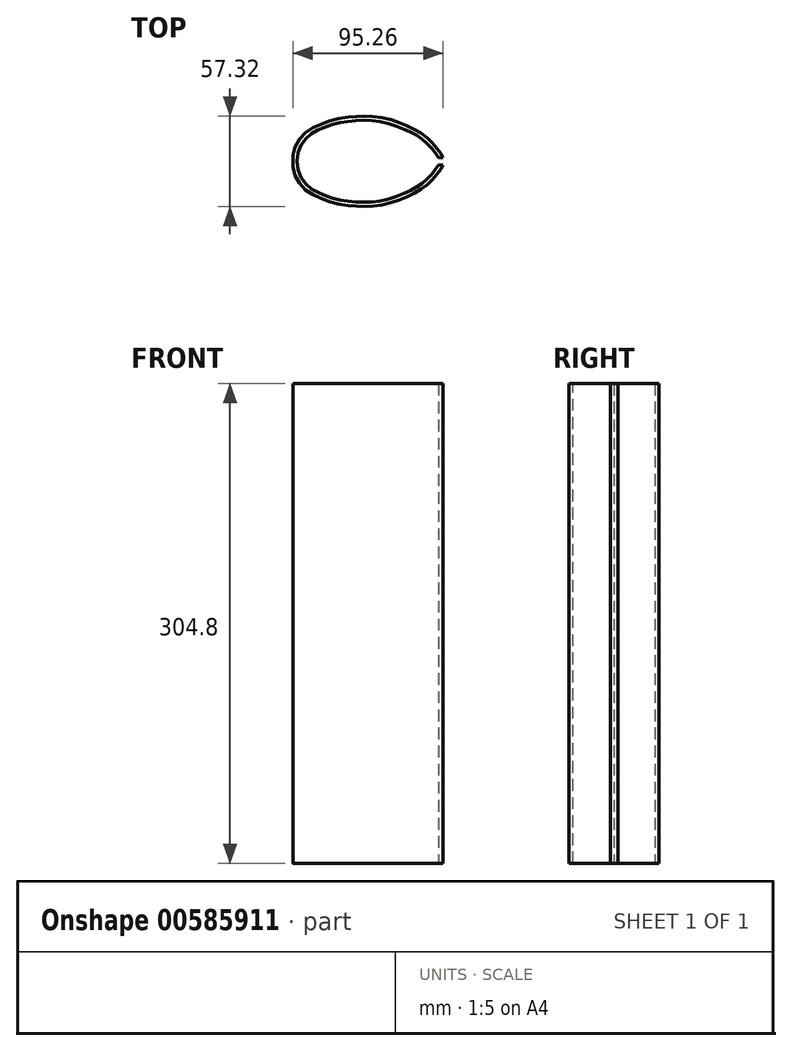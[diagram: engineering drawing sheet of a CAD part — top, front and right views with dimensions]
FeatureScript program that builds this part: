
annotation { "Feature Type Name" : "Feature", "Feature Type Description" : "" }
export const myFeature = defineFeature(function(context is Context, id is Id, definition is map)
    precondition{}
    {
        {
            var Q0;
            Q0=qCreatedBy(makeId("Top.planeOp"),FACE);
            var sketch = newSketch(context, id + "F0", { "sketchPlane" : qUnion([Q0])});
            skPoint(sketch, "E0", {"position": v(-43.82, 0) * mm});
            skSolve(sketch);
        }
        {
            var Q0;
            Q0=qCreatedBy(makeId("Top.planeOp"),FACE);
            var sketch = newSketch(context, id + "F1", { "sketchPlane" : qUnion([Q0])});
            skPoint(sketch, "E1", {"position": v(51.44, 0) * mm});
            skSolve(sketch);
        }
        {
            var Q0;
            Q0=qCreatedBy(makeId("Top.planeOp"),FACE);
            var sketch = newSketch(context, id + "F2", { "sketchPlane" : qUnion([Q0])});
            skPoint(sketch, "E2", {"position": v(0, 28.58) * mm});
            skSolve(sketch);
        }
        {
            var Q0;
            Q0=qCreatedBy(makeId("Top.planeOp"),FACE);
            var sketch = newSketch(context, id + "F3", { "sketchPlane" : qUnion([Q0])});
            skPoint(sketch, "E3", {"position": v(22.07, 0) * mm});
            skSolve(sketch);
        }
        {
            var Q0;
            Q0=qCreatedBy(makeId("Top.planeOp"),FACE);
            var sketch = newSketch(context, id + "F4", { "sketchPlane" : qUnion([Q0])});
            skPoint(sketch, "E4", {"position": v(14.86, 19.05) * mm});
            skSolve(sketch);
        }
        {
            var Q0;
            Q0=qCreatedBy(makeId("Top.planeOp"),FACE);
            var sketch = newSketch(context, id + "F5", { "sketchPlane" : qUnion([Q0])});
            skPoint(sketch, "E5", {"position": v(51.44, 2.39) * mm});
            skSolve(sketch);
        }
        {
            var Q0;
            Q0=qCreatedBy(makeId("Top.planeOp"),FACE);
            var sketch = newSketch(context, id + "F6", { "sketchPlane" : qUnion([Q0])});
            skArc(sketch, "E6", {"start": v(0, 28.58) * mm, "mid": v(-19.2, 25.91) * mm, "end": v(-36.96, 18.13) * mm});
            skSolve(sketch);
        }
        {
            var Q0;
            Q0=qCreatedBy(makeId("Top.planeOp"),FACE);
            var sketch = newSketch(context, id + "F7", { "sketchPlane" : qUnion([Q0])});
            skPoint(sketch, "E7", {"position": v(0, 25.04) * mm});
            skSolve(sketch);
        }
        {
            var Q0;
            Q0=qCreatedBy(makeId("Top.planeOp"),FACE);
            var sketch = newSketch(context, id + "F8", { "sketchPlane" : qUnion([Q0])});
            skLineSegment(sketch, "E8.bottom", {"start": v(46.93, 0) * mm, "end": v(59.21, 0) * mm});
            skLineSegment(sketch, "E8.top", {"start": v(46.93, 2.39) * mm, "end": v(59.21, 2.39) * mm});
            skLineSegment(sketch, "E8.left", {"start": v(46.93, 0) * mm, "end": v(46.93, 2.39) * mm});
            skLineSegment(sketch, "E8.right", {"start": v(59.21, 0) * mm, "end": v(59.21, 2.39) * mm});
            skSolve(sketch);
        }
        {
            var Q0;
            Q0=qCreatedBy(makeId("Top.planeOp"),FACE);
            var sketch = newSketch(context, id + "F9", { "sketchPlane" : qUnion([Q0])});
            skFitSpline(sketch, "E9", {"points": [v(-43.82, 0) * mm, v(-42.29, 8.43) * mm, v(-38.7, 14.76) * mm, v(-33.64, 19.55) * mm, v(-28, 22.56) * mm, v(-21.88, 24.98) * mm, v(-13.72, 27.17) * mm, v(-5.78, 28.23) * mm, v(0, 28.56) * mm, v(5.9, 28.37) * mm, v(12.54, 27.57) * mm, v(19.9, 25.73) * mm, v(25.6, 23.7) * mm, v(31.67, 20.94) * mm, v(36.27, 18.37) * mm, v(40.88, 15.08) * mm, v(44.19, 12) * mm, v(47.1, 8.7) * mm, v(49.61, 5.46) * mm, v(51.44, 2.39) * mm], "startDerivative": vector(2.54, 145.05) * mm, "endDerivative": vector(28.25, -58.97) * mm});
            skSolve(sketch);
        }
        {
            var Q0;
            Q0=qCreatedBy(makeId("Top.planeOp"),FACE);
            var sketch = newSketch(context, id + "F10", { "sketchPlane" : qUnion([Q0])});
            skFitSpline(sketch, "E10.0", {"points": [v(-41.28, 0.01) * mm, v(-41.28, 1.36) * mm, v(-41.03, 4) * mm, v(-40.15, 7.05) * mm, v(-39.2, 9.27) * mm, v(-38.37, 10.83) * mm, v(-37.4, 12.3) * mm, v(-36.33, 13.7) * mm, v(-35.14, 15) * mm, v(-33.86, 16.2) * mm, v(-32.73, 17.1) * mm, v(-31.81, 17.72) * mm, v(-30.86, 18.32) * mm, v(-29.62, 19) * mm, v(-28.3, 19.64) * mm, v(-27.23, 20.13) * mm, v(-26.13, 20.61) * mm, v(-24.77, 21.2) * mm, v(-23.09, 21.86) * mm, v(-21.33, 22.5) * mm, v(-19.46, 23.1) * mm, v(-17.5, 23.69) * mm, v(-15.47, 24.21) * mm, v(-13.76, 24.59) * mm, v(-12.4, 24.84) * mm, v(-11.02, 25.07) * mm, v(-9.32, 25.31) * mm, v(-7.32, 25.54) * mm, v(-5.4, 25.72) * mm, v(-3.63, 25.87) * mm, v(-1.94, 25.97) * mm, v(-0.3, 26.03) * mm, v(1.37, 26.03) * mm, v(3.08, 25.99) * mm, v(4.84, 25.9) * mm, v(6.62, 25.78) * mm, v(8.4, 25.61) * mm, v(10.2, 25.39) * mm, v(12.04, 25.1) * mm, v(13.96, 24.7) * mm, v(15.9, 24.22) * mm, v(17.81, 23.7) * mm, v(19.62, 23.16) * mm, v(21.27, 22.62) * mm, v(22.87, 22.06) * mm, v(24.47, 21.43) * mm, v(26.17, 20.71) * mm, v(27.9, 19.94) * mm, v(29.32, 19.27) * mm, v(30.39, 18.75) * mm, v(31.4, 18.23) * mm, v(32.59, 17.6) * mm, v(33.71, 16.96) * mm, v(34.62, 16.41) * mm, v(35.54, 15.83) * mm, v(36.71, 15.04) * mm, v(37.86, 14.22) * mm, v(38.73, 13.55) * mm, v(39.56, 12.9) * mm, v(40.49, 12.1) * mm, v(41.51, 11.12) * mm, v(42.5, 10.1) * mm, v(43.5, 9) * mm, v(44.33, 8.04) * mm, v(44.98, 7.28) * mm, v(45.61, 6.52) * mm, v(46.2, 5.8) * mm, v(46.77, 5.07) * mm, v(47.18, 4.52) * mm, v(47.57, 3.95) * mm, v(47.96, 3.36) * mm, v(48.33, 2.77) * mm, v(48.67, 2.2) * mm, v(48.95, 1.68) * mm, v(49.09, 1.4) * mm, v(49.14, 1.3) * mm]});
            skSolve(sketch);
        }
        {
            var Q0;
            Q0=qCreatedBy(makeId("Top.planeOp"),FACE);
            var sketch = newSketch(context, id + "F11", { "sketchPlane" : qUnion([Q0])});
            skArc(sketch, "E11", {"start": v(28.78, 19.52) * mm, "mid": v(23.8, 10.32) * mm, "end": v(22.07, 0) * mm});
            skSolve(sketch);
        }
        {
            var Q0;
            Q0=qCreatedBy(makeId("Top.planeOp"),FACE);
            var sketch = newSketch(context, id + "F12", { "sketchPlane" : qUnion([Q0])});
            skArc(sketch, "E12.0", {"start": v(31.12, 18.38) * mm, "mid": v(26.29, 9.75) * mm, "end": v(24.61, 0) * mm});
            skSolve(sketch);
        }
        {
            var Q0;
            Q0=qCreatedBy(makeId("Top.planeOp"),FACE);
            var sketch = newSketch(context, id + "F13", { "sketchPlane" : qUnion([Q0])});
            skLineSegment(sketch, "E13", {"start": v(-11.16, 25.04) * mm, "end": v(12.21, 25.04) * mm});
            skSolve(sketch);
        }
        {
            var Q0;
            Q0=qCreatedBy(makeId("Top.planeOp"),FACE);
            var sketch = newSketch(context, id + "F14", { "sketchPlane" : qUnion([Q0])});
            skLineSegment(sketch, "E14", {"start": v(48.55, 2.39) * mm, "end": v(51.44, 2.39) * mm});
            skSolve(sketch);
        }
        {
            var Q0;
            Q0=qCreatedBy(makeId("Top.planeOp"),FACE);
            var sketch = newSketch(context, id + "F15", { "sketchPlane" : qUnion([Q0])});
            skLineSegment(sketch, "E15", {"start": v(-43.82, 0) * mm, "end": v(-41.27, 0) * mm});
            skSolve(sketch);
        }
        {
            var Q0;
            Q0=qCreatedBy(makeId("Top.planeOp"),FACE);
            var sketch = newSketch(context, id + "F16", { "sketchPlane" : qUnion([Q0])});
            skLineSegment(sketch, "E16", {"start": v(24.61, 0) * mm, "end": v(22.07, 0) * mm});
            skSolve(sketch);
        }
        {
            var Q0;
            Q0=qCreatedBy(makeId("Top.planeOp"),FACE);
            var sketch = newSketch(context, id + "F17", { "sketchPlane" : qUnion([Q0])});
            skLineSegment(sketch, "E17", {"start": v(-41.27, 0) * mm, "end": v(-41.27, 0.01) * mm});
            skSolve(sketch);
        }
        {
            var Q0;
            Q0=qCreatedBy(makeId("Top.planeOp"),FACE);
            var sketch = newSketch(context, id + "F18", { "sketchPlane" : qUnion([Q0])});
            skLineSegment(sketch, "E18.0", {"start": v(-41.27, 0) * mm, "end": v(-41.27, 0.01) * mm});
            skLineSegment(sketch, "E19.0", {"start": v(-43.82, 0) * mm, "end": v(-41.27, 0) * mm});
            skFitSpline(sketch, "E20.0", {"points": [v(-43.82, 0) * mm, v(-43.76, 3) * mm, v(-42.74, 8.52) * mm, v(-39, 14.92) * mm, v(-33.86, 19.83) * mm, v(-27.97, 22.64) * mm, v(-21.87, 25.13) * mm, v(-13.8, 27.4) * mm, v(-5.87, 28.28) * mm, v(-0.05, 28.66) * mm, v(6, 28.43) * mm, v(12.54, 27.76) * mm, v(19.96, 25.8) * mm, v(25.53, 23.83) * mm, v(31.74, 21) * mm, v(36.24, 18.5) * mm, v(40.96, 15.18) * mm, v(44.2, 12.1) * mm, v(47.12, 8.7) * mm, v(49.6, 5.66) * mm, v(51.06, 3.18) * mm, v(51.44, 2.39) * mm]});
            skFitSpline(sketch, "E21.0", {"points": [v(-41.28, -0.04) * mm, v(-41.25, 1.33) * mm, v(-41.05, 3.34) * mm, v(-40.48, 5.85) * mm, v(-39.91, 7.62) * mm, v(-39.2, 9.27) * mm, v(-38.37, 10.82) * mm, v(-37.41, 12.3) * mm, v(-36.33, 13.7) * mm, v(-35.13, 15) * mm, v(-33.85, 16.2) * mm, v(-32.73, 17.1) * mm, v(-31.81, 17.72) * mm, v(-30.86, 18.32) * mm, v(-29.62, 19) * mm, v(-28.3, 19.64) * mm, v(-27.23, 20.13) * mm, v(-26.13, 20.61) * mm, v(-24.76, 21.2) * mm, v(-23.09, 21.86) * mm, v(-21.33, 22.5) * mm, v(-19.46, 23.1) * mm, v(-17.5, 23.69) * mm, v(-15.47, 24.21) * mm, v(-13.76, 24.59) * mm, v(-12.4, 24.84) * mm, v(-11.02, 25.07) * mm, v(-9.32, 25.31) * mm, v(-7.32, 25.54) * mm, v(-5.4, 25.72) * mm, v(-3.63, 25.87) * mm, v(-1.94, 25.97) * mm, v(-0.3, 26.03) * mm, v(1.37, 26.03) * mm, v(3.08, 25.99) * mm, v(4.84, 25.9) * mm, v(6.62, 25.78) * mm, v(8.4, 25.61) * mm, v(10.2, 25.39) * mm, v(12.04, 25.1) * mm, v(13.96, 24.7) * mm, v(15.9, 24.22) * mm, v(17.81, 23.7) * mm, v(19.62, 23.16) * mm, v(21.27, 22.62) * mm, v(22.87, 22.06) * mm, v(24.47, 21.43) * mm, v(26.17, 20.71) * mm, v(27.9, 19.94) * mm, v(29.32, 19.27) * mm, v(30.39, 18.75) * mm, v(31.4, 18.23) * mm, v(32.59, 17.6) * mm, v(33.71, 16.96) * mm, v(34.62, 16.41) * mm, v(35.54, 15.83) * mm, v(36.71, 15.04) * mm, v(37.86, 14.22) * mm, v(38.73, 13.55) * mm, v(39.56, 12.9) * mm, v(40.49, 12.1) * mm, v(41.51, 11.12) * mm, v(42.5, 10.1) * mm, v(43.5, 9) * mm, v(44.33, 8.04) * mm, v(44.98, 7.28) * mm, v(45.61, 6.52) * mm, v(46.2, 5.8) * mm, v(46.77, 5.07) * mm, v(47.18, 4.52) * mm, v(47.57, 3.95) * mm, v(47.96, 3.36) * mm, v(48.33, 2.77) * mm, v(48.67, 2.2) * mm, v(48.95, 1.68) * mm, v(49.09, 1.4) * mm, v(49.14, 1.3) * mm]});
            skLineSegment(sketch, "E22.0", {"start": v(-11.16, 25.04) * mm, "end": v(12.21, 25.04) * mm});
            skArc(sketch, "E23.0", {"start": v(28.78, 19.52) * mm, "mid": v(23.8, 10.32) * mm, "end": v(22.07, 0) * mm});
            skArc(sketch, "E24.0", {"start": v(31.12, 18.38) * mm, "mid": v(26.29, 9.75) * mm, "end": v(24.61, 0) * mm});
            skLineSegment(sketch, "E25.0", {"start": v(24.61, 0) * mm, "end": v(22.07, 0) * mm});
            skLineSegment(sketch, "E26.0", {"start": v(48.55, 2.39) * mm, "end": v(51.44, 2.39) * mm});
            skSolve(sketch);
        }
        {
            var Q0;
            Q0 = qSketchRegion(id + "F18", true);
            extrude(context, id + "F19", {"entities" : qUnion([Q0]), "depth" : 304.8 * mm, "offsetDistance" : 25.4 * mm, "symmetric" : true});
        }
        {
            var Q0;
            Q0=makeQuery(id+"F19.opExtrude","SWEPT_BODY",BODY,{"disambiguationData":[OSD([sQuery(id+"F18.wireOp",EDGE,"E18.0"),sQuery(id+"F18.wireOp",EDGE,"E19.0"),sQuery(id+"F18.wireOp",EDGE,"E20.0"),sQuery(id+"F18.wireOp",EDGE,"E21.0"),sQuery(id+"F18.wireOp",EDGE,"E22.0"),sQuery(id+"F18.wireOp",EDGE,"E23.0"),sQuery(id+"F18.wireOp",EDGE,"E24.0"),sQuery(id+"F18.wireOp",EDGE,"E25.0"),sQuery(id+"F18.wireOp",EDGE,"E26.0")])]});
            var Q1;
            Q1=qCreatedBy(makeId("Front.planeOp"),FACE);
            mirror(context, id + "F20", {"operationType" : NewBodyOperationType.ADD, "entities" : qUnion([Q0]), "mirrorPlane" : qUnion([Q1])});
        }
    });
